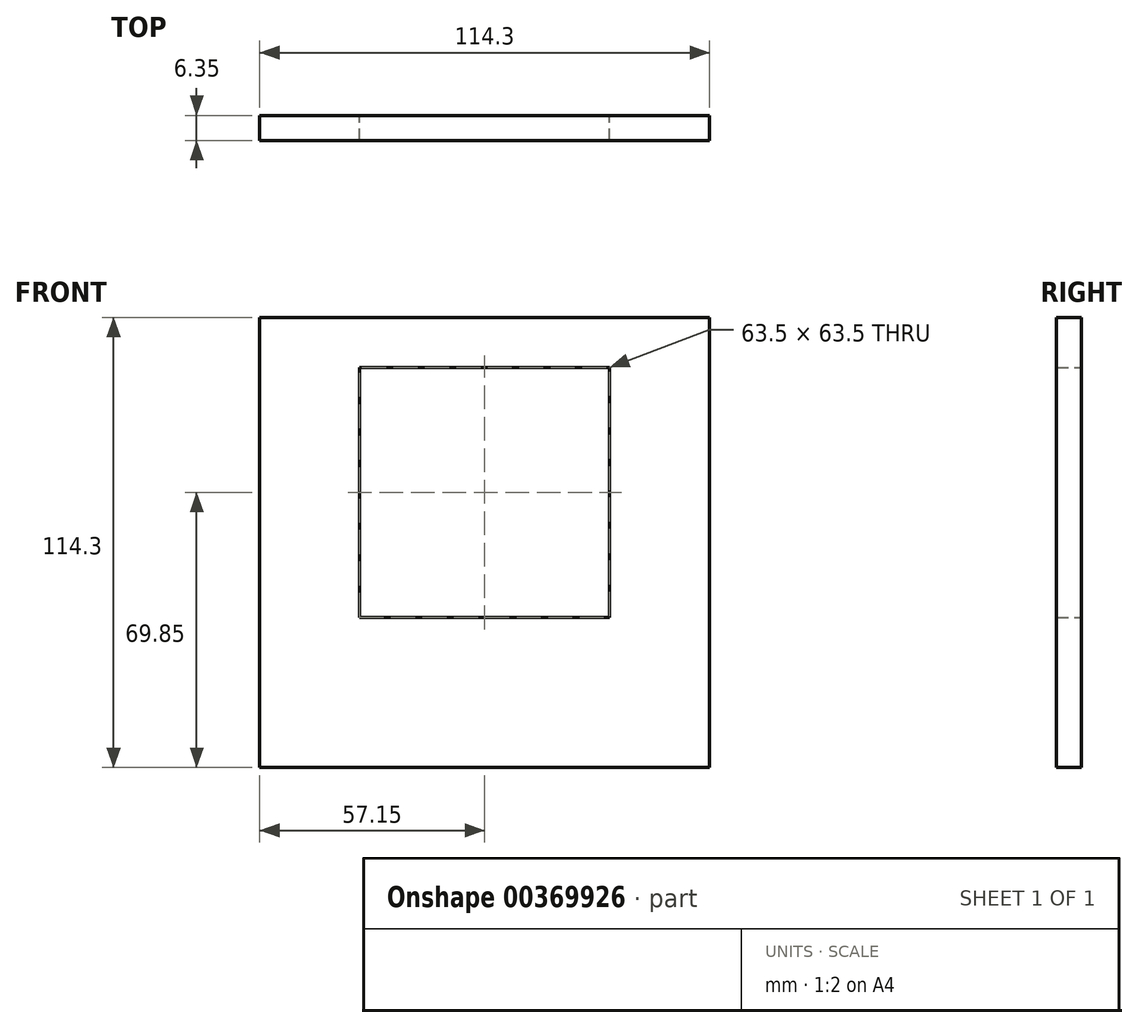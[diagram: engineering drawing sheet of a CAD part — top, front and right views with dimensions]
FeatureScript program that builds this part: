
annotation { "Feature Type Name" : "Feature", "Feature Type Description" : "" }
export const myFeature = defineFeature(function(context is Context, id is Id, definition is map)
    precondition{}
    {
        {
            var Q0;
            Q0=qCreatedBy(makeId("Front.planeOp"),FACE);
            var sketch = newSketch(context, id + "F0", { "sketchPlane" : qUnion([Q0])});
            skLineSegment(sketch, "E0.bottom", {"start": v(0, 0) * mm, "end": v(114.3, 0) * mm});
            skLineSegment(sketch, "E0.top", {"start": v(0, 114.3) * mm, "end": v(114.3, 114.3) * mm});
            skLineSegment(sketch, "E0.left", {"start": v(0, 0) * mm, "end": v(0, 114.3) * mm});
            skLineSegment(sketch, "E0.right", {"start": v(114.3, 0) * mm, "end": v(114.3, 114.3) * mm});
            skLineSegment(sketch, "E1.bottom", {"start": v(25.4, 38.1) * mm, "end": v(88.9, 38.1) * mm});
            skLineSegment(sketch, "E1.top", {"start": v(25.4, 101.6) * mm, "end": v(88.9, 101.6) * mm});
            skLineSegment(sketch, "E1.left", {"start": v(25.4, 38.1) * mm, "end": v(25.4, 101.6) * mm});
            skLineSegment(sketch, "E1.right", {"start": v(88.9, 38.1) * mm, "end": v(88.9, 101.6) * mm});
            skSolve(sketch);
        }
        {
            var Q0;
            Q0 = qSketchRegion(id + "F0", true);
            extrude(context, id + "F1", {"entities" : qUnion([Q0]), "depth" : 6.35 * mm});
        }
    });
